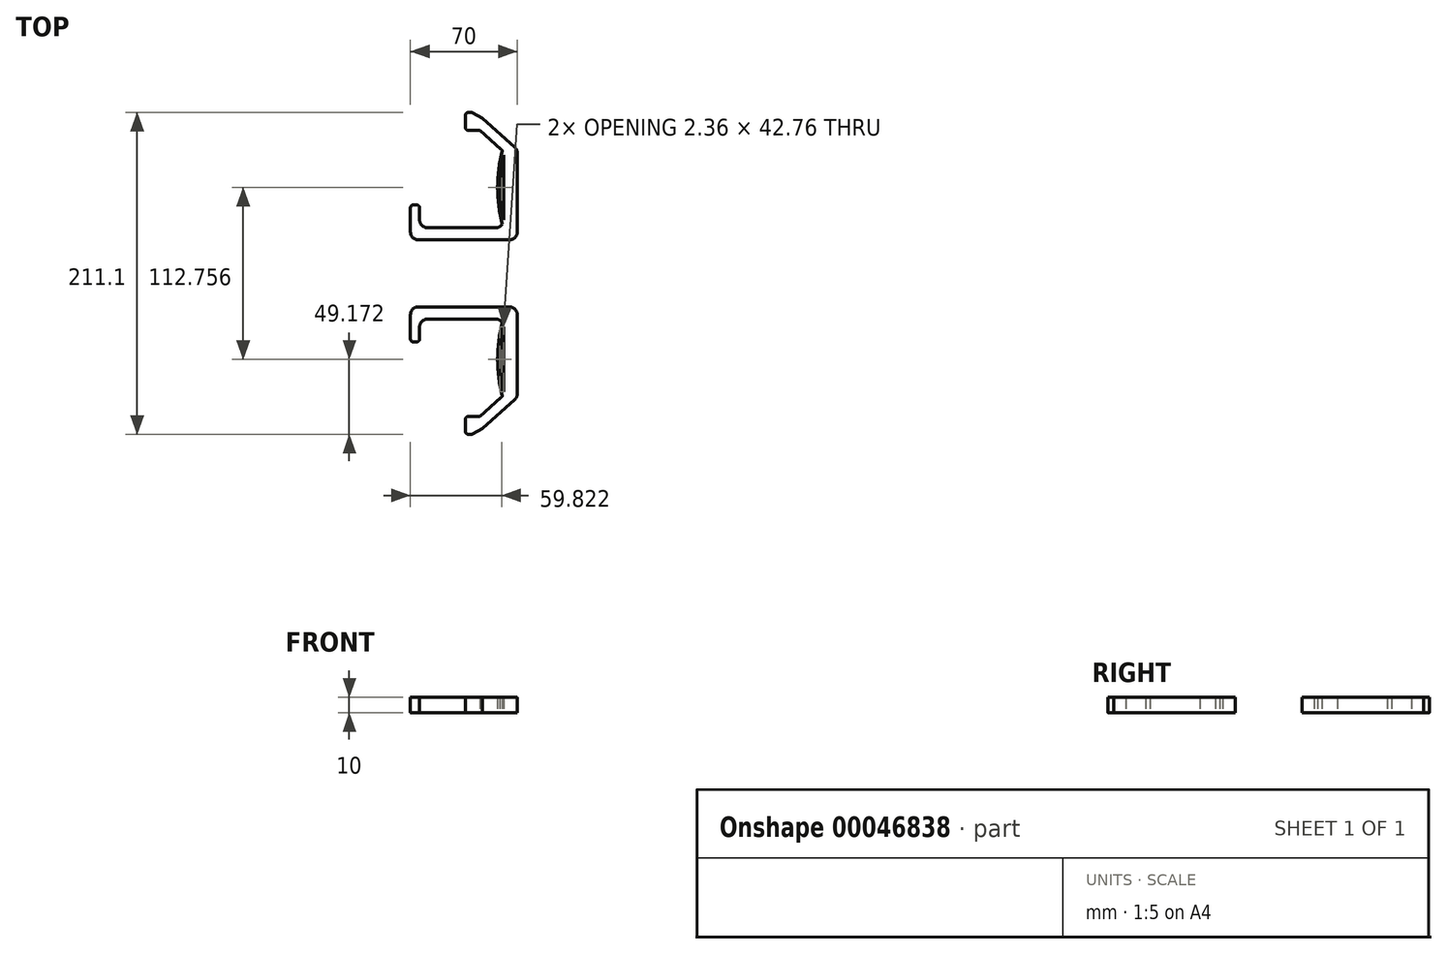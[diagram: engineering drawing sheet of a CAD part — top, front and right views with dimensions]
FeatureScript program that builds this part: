
annotation { "Feature Type Name" : "Feature", "Feature Type Description" : "" }
export const myFeature = defineFeature(function(context is Context, id is Id, definition is map)
    precondition{}
    {
        {
            var Q0;
            Q0=qCreatedBy(makeId("Top.planeOp"),FACE);
            var sketch = newSketch(context, id + "F0", { "sketchPlane" : qUnion([Q0])});
            skLineSegment(sketch, "E0", {"start": v(0, 13) * mm, "end": v(0, 5) * mm});
            skLineSegment(sketch, "E1", {"start": v(5, 0) * mm, "end": v(50, 0) * mm});
            skLineSegment(sketch, "E2", {"start": v(55, 5) * mm, "end": v(55, 47.76) * mm});
            skLineSegment(sketch, "E3", {"start": v(53.32, 51.5) * mm, "end": v(39.54, 63.76) * mm});
            skLineSegment(sketch, "E4.1", {"start": v(-6, 13) * mm, "end": v(-6, -3) * mm});
            skLineSegment(sketch, "E4.2", {"start": v(-1, -8) * mm, "end": v(59, -8) * mm});
            skLineSegment(sketch, "E4.3", {"start": v(64, -3) * mm, "end": v(64, 49.12) * mm});
            skLineSegment(sketch, "E4.4", {"start": v(62.32, 52.85) * mm, "end": v(41.12, 71.72) * mm});
            skLineSegment(sketch, "E5", {"start": v(-4, 15) * mm, "end": v(-2, 15) * mm});
            skPoint(sketch, "E6.visualSharp", {"position": v(-6, -8) * mm});
            skArc(sketch, "E6.filletArc", {"start": v(-6, -3) * mm, "mid": v(-4.54, -6.54) * mm, "end": v(-1, -8) * mm});
            skPoint(sketch, "E7.visualSharp", {"position": v(64, -8) * mm});
            skArc(sketch, "E7.filletArc", {"start": v(59, -8) * mm, "mid": v(62.54, -6.54) * mm, "end": v(64, -3) * mm});
            skPoint(sketch, "E8.visualSharp", {"position": v(64, 51.36) * mm});
            skArc(sketch, "E8.filletArc", {"start": v(64, 49.12) * mm, "mid": v(63.56, 51.16) * mm, "end": v(62.32, 52.85) * mm});
            skPoint(sketch, "E9.visualSharp", {"position": v(39.7, 72.99) * mm});
            skPoint(sketch, "E10.visualSharp", {"position": v(0, 0) * mm});
            skArc(sketch, "E10.filletArc", {"start": v(0, 5) * mm, "mid": v(1.46, 1.46) * mm, "end": v(5, 0) * mm});
            skPoint(sketch, "E11.visualSharp", {"position": v(55, 0) * mm});
            skArc(sketch, "E11.filletArc", {"start": v(50, 0) * mm, "mid": v(52.33, 0.58) * mm, "end": v(54.13, 2.18) * mm});
            skPoint(sketch, "E12.visualSharp", {"position": v(35.9, 67) * mm});
            skPoint(sketch, "E13.visualSharp", {"position": v(55, 50) * mm});
            skArc(sketch, "E13.filletArc", {"start": v(54.13, 50.58) * mm, "mid": v(53.75, 51.06) * mm, "end": v(53.32, 51.5) * mm});
            skLineSegment(sketch, "E14", {"start": v(30, 66.59) * mm, "end": v(30, 71.5) * mm});
            skArc(sketch, "E15", {"start": v(55, 47.76) * mm, "mid": v(52.64, 26.38) * mm, "end": v(55, 5) * mm});
            skArc(sketch, "E16.0", {"start": v(54.13, 50.58) * mm, "mid": v(51.14, 26.38) * mm, "end": v(54.13, 2.18) * mm});
            skLineSegment(sketch, "E17.bottom", {"start": v(32, 75.55) * mm, "end": v(34.43, 75.55) * mm});
            skLineSegment(sketch, "E17.top", {"start": v(32, 63.76) * mm, "end": v(33.1, 63.76) * mm});
            skLineSegment(sketch, "E17.left", {"start": v(30, 73.55) * mm, "end": v(30, 65.76) * mm});
            skLineSegment(sketch, "E18", {"start": v(33.1, 63.76) * mm, "end": v(39.54, 63.76) * mm});
            skLineSegment(sketch, "E19", {"start": v(34.43, 75.55) * mm, "end": v(41.12, 71.72) * mm});
            skPoint(sketch, "E20.visualSharp", {"position": v(-6, 15) * mm});
            skArc(sketch, "E20.filletArc", {"start": v(-4, 15) * mm, "mid": v(-5.41, 14.41) * mm, "end": v(-6, 13) * mm});
            skPoint(sketch, "E21.visualSharp", {"position": v(0, 15) * mm});
            skArc(sketch, "E21.filletArc", {"start": v(0, 13) * mm, "mid": v(-0.59, 14.41) * mm, "end": v(-2, 15) * mm});
            skPoint(sketch, "E22.visualSharp", {"position": v(30, 63.76) * mm});
            skArc(sketch, "E22.filletArc", {"start": v(30, 65.76) * mm, "mid": v(30.59, 64.34) * mm, "end": v(32, 63.76) * mm});
            skPoint(sketch, "E23.visualSharp", {"position": v(30, 75.55) * mm});
            skArc(sketch, "E23.filletArc", {"start": v(32, 75.55) * mm, "mid": v(30.59, 74.96) * mm, "end": v(30, 73.55) * mm});
            skSolve(sketch);
        }
        {
            var Q0;
            Q0=makeQuery(id+"F0.imprint","IMPRINT",FACE,{"disambiguationData":[TD([[makeQuery(id+"F0.imprint","IMPRINT",EDGE,{"derivedFrom":sQuery(id+"F0.wireOp",EDGE,"E0")}),-1.0]])]});
            extrude(context, id + "F1", {"entities" : qUnion([Q0]), "depth" : 10 * mm});
        }
        {
            var Q0;
            Q0=makeQuery(id+"F1.opExtrude","SWEPT_EDGE",EDGE,{"disambiguationData":[OSD([sQuery(id+"F0.wireOp",EDGE,"E17.top"),sQuery(id+"F0.wireOp",EDGE,"E17.left")])]});
            var Q1;
            Q1=makeQuery(id+"F1.opExtrude","SWEPT_EDGE",EDGE,{"disambiguationData":[OSD([sQuery(id+"F0.wireOp",EDGE,"E17.bottom"),sQuery(id+"F0.wireOp",EDGE,"E17.left")])]});
            fillet(context, id + "F2", {"entities" : qUnion([Q0, Q1]), "radius" : 2 * mm, "tangentPropagation" : true, "allowEdgeOverflow" : false});
        }
        {
            var Q0;
            Q0=qCreatedBy(makeId("Front.planeOp"),FACE);
            cPlane(context, id + "F3", {"entities" : qUnion([Q0]), "cplaneType" : CPlaneType.OFFSET, "offset" : 30 * mm, "width" : 150 * mm, "height" : 150 * mm});
        }
        {
            var Q0;
            Q0=makeQuery(id+"F1.opExtrude","SWEPT_BODY",BODY,{"disambiguationData":[OSD([sQuery(id+"F0.wireOp",EDGE,"E0"),sQuery(id+"F0.wireOp",EDGE,"E1"),sQuery(id+"F0.wireOp",EDGE,"E2"),sQuery(id+"F0.wireOp",EDGE,"E3"),sQuery(id+"F0.wireOp",EDGE,"E4.1"),sQuery(id+"F0.wireOp",EDGE,"E4.2"),sQuery(id+"F0.wireOp",EDGE,"E4.3"),sQuery(id+"F0.wireOp",EDGE,"E4.4"),sQuery(id+"F0.wireOp",EDGE,"E5"),sQuery(id+"F0.wireOp",EDGE,"E6.filletArc"),sQuery(id+"F0.wireOp",EDGE,"E7.filletArc"),sQuery(id+"F0.wireOp",EDGE,"E8.filletArc"),sQuery(id+"F0.wireOp",EDGE,"E10.filletArc"),sQuery(id+"F0.wireOp",EDGE,"E11.filletArc"),sQuery(id+"F0.wireOp",EDGE,"E13.filletArc"),sQuery(id+"F0.wireOp",EDGE,"E15"),sQuery(id+"F0.wireOp",EDGE,"E16.0"),sQuery(id+"F0.wireOp",EDGE,"E17.bottom"),sQuery(id+"F0.wireOp",EDGE,"E17.top"),sQuery(id+"F0.wireOp",EDGE,"E17.left"),sQuery(id+"F0.wireOp",EDGE,"E18"),sQuery(id+"F0.wireOp",EDGE,"E19"),sQuery(id+"F0.wireOp",EDGE,"E20.filletArc"),sQuery(id+"F0.wireOp",EDGE,"E21.filletArc"),sQuery(id+"F0.wireOp",EDGE,"E22.filletArc"),sQuery(id+"F0.wireOp",EDGE,"E23.filletArc")])]});
            var Q1;
            Q1=qCreatedBy(id+"F3.planeOp",FACE);
            mirror(context, id + "F4", {"entities" : qUnion([Q0]), "mirrorPlane" : qUnion([Q1])});
        }
    });
